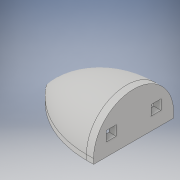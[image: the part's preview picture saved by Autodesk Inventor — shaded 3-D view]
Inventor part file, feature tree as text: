
AUTODESK INVENTOR PART (.ipt)
format: ipt  version: 2019 (Build 230136000, 136)  size: 180,736 bytes
history: native  units: in
note: dims shown in document units (in); Inventor stores cm internally (conversion verified against a paired STEP export)
features: extrude x2, sketch x2, projected_geometry x2, revolve x1
ambient origin geometry x8: Origin, YZ Plane, XZ Plane, XY Plane, X Axis, Y Axis, Z Axis, Center Point
bodies: Solid1 (feature_tree)
feature tree (7):
  revolve  "Revolution1"  [1 undecoded]
  extrude  "Extrusion2"  Depth=3.9449in
  extrude  "Extrusion3"  TaperAngle=180.0deg  [1 undecoded]
  sketch  "Sketch3"  dims[d13=0.25in d15=1.9724in]
  sketch  "Sketch4"  dims[d16=0.25in d17=3.9449in d18=180.0deg d21=2.0in d23=1.0in d24=0.25in d26=0.25in d27=0.0in d28=0.4924in d29=0.4924in d30=0.8576in d31=0.35in d32=0.0in]
  projected_geometry  "Projected Loop1"
  projected_geometry  "Projected Loop2"
note: 2 required parameter values undecoded (feature->parameter linkage not recoverable at this tier; creation-order binding heuristic only, values carry confidence <= 0.55)